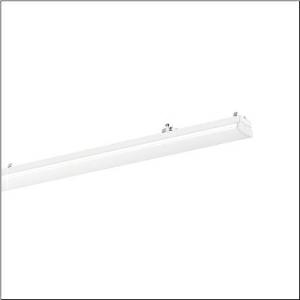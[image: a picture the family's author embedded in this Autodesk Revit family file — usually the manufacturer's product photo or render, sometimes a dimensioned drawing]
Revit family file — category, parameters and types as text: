
# Revit family: licross_21_recessed_opal_mo_52tl1ddv495g
name_source: partatom
category: Lighting Fixtures
units: mm (PartAtom-declared; Revit-internal decimal feet)

## family parameters
Cut with Voids When Loaded = No
Host = Face
Light Source = No
Part Type = Normal
Room Calculation Point = No
Round Connector Dimension = Use Diameter
Shared = No

## types (1)
- --- (1 x LED, 9500 lm, 53.6 W, 4000K)
    Apparent Load = 54 VA
    CIE Flux Codes = 44 73 91 87 100
    Color Rendering = 80
    Color Temperature = 4000K
    Default Elevation = 1800 mm
    Description = Licross 21 recessed opal MO, luminaire insert, of sheet steel, galvanised, coil coated, white, length: 2.250mm, width: 66mm, height: 67mm, LED rated luminous flux: 9.500lm, light colour: 840, SDCM (Standard Deviation of Colour Matching)MacAdam ≤ 3 SDCM (initial), control gear: DALI 2, with plug, 5-pole, with phase selection, mains connection: 220..240V, AC, 50/60Hz, rated input power: 54W, internal wiring halogen-free, primary optical cover: cover, of PMMA, light emission: direct with ceiling illumination distribution, primary light characteristic: symmetric, protection rating (complete): IP40, insulation class (complete): insulation class I (protective earthing), certification: CE, ENEC, VDE, UKCA, protection symbol: D if used in an environment without relevant dust loads with corresponding accessories, impact resistance: IK06, permissible ambient temperature for indoor applications: -25..+40°C, corresponds to IFS (International Featured Standards) requirements for safety and quality in the food industry, reducing of maximum allowable ambient temperature of 5°C with ceiling mounting, LABS conformity tested according to VDMA 24364:2018-05, The light source and the operating device comply with the requirements of the Ecodesign Regulation (EU) 2019/2020 and are replaceable in accordance with this regulation, packaging unit: 1 piece
    Height = 83 mm
    Lamp = 1 x LED
    Lamp Light Flux = 9500 lm
    Lamp Power = 53.6 W
    Lamp count = 1
    Length = 2250 mm
    Luminous efficacy = 177 lm/W
    Manufacturer = Siteco
    ModVariant = No
    Model = 52TL1DDV495G
    Mounting Place = Ceiling
    Mounting Type = Pendant
    Number of Poles = 1
    OnlyDefault = Yes
    Power Factor = 1
    Product Name = Licross 21 recessed opal MO
    Product group = luminaire insert | ceiling pendant
    ProductGroupID = 901
    Protection Class = Protection class I
    Protection Degree = IP 40
    RLX_Detail_Level = 1
    RLX_Emergency_Light_Flux = 0 lm
    RLX_Emergency_Type = 0
    RLX_Emergency_Type_DB = No
    RlxData = <blob elided: 26857 chars, md5=a9a44f26>
    Socket = socket
    Standby Power = 0 W
    System Light Flux = 9500 lm
    System Power = 54 W
    Type Comments = factory setting: luminous flux: 100 % | dim-lin: 254 | 246 mA
    Type Image = l_1313666.jpg
    URL = http://relux.com
    VarID = @adj_072401
    Voltage = 0 V
    Weight = 0.00 kg
    Width = 76 mm

## geometry (parser evidence)
native form markers: Blend x4, Sweep x12
no freeform markers — native parametric forms only
